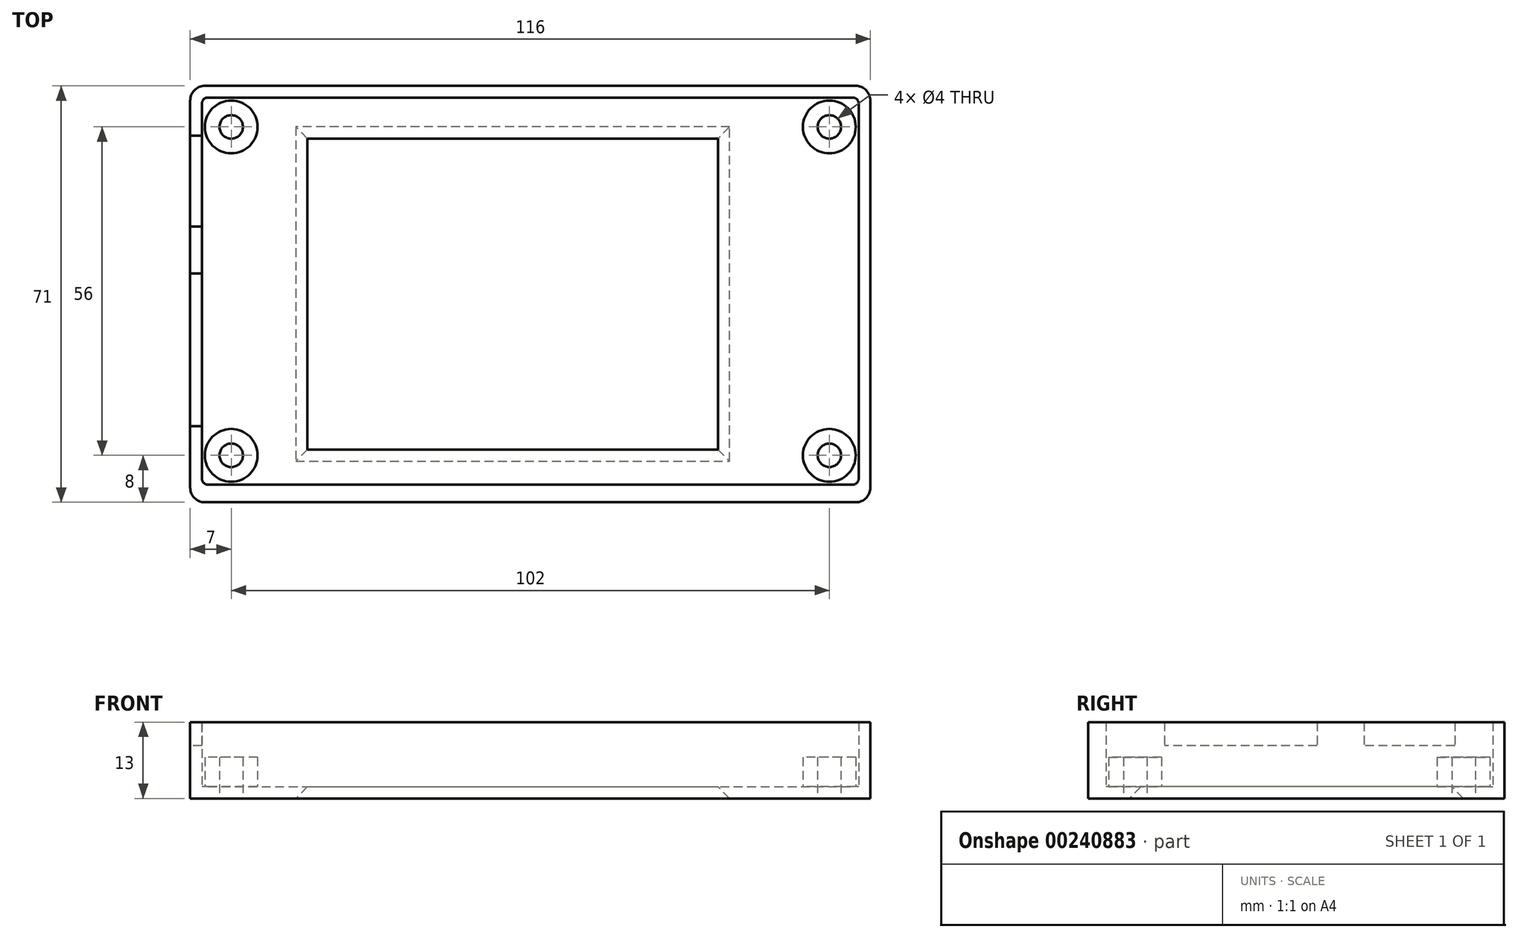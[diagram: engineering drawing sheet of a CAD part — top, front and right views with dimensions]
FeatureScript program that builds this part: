
annotation { "Feature Type Name" : "Feature", "Feature Type Description" : "" }
export const myFeature = defineFeature(function(context is Context, id is Id, definition is map)
    precondition{}
    {
        {
            var Q0;
            Q0=qCreatedBy(makeId("Top.planeOp"),FACE);
            var sketch = newSketch(context, id + "F0", { "sketchPlane" : qUnion([Q0])});
            skLineSegment(sketch, "E0.bottom", {"start": v(0, 71) * mm, "end": v(116, 71) * mm});
            skLineSegment(sketch, "E0.top", {"start": v(0, 0) * mm, "end": v(116, 0) * mm});
            skLineSegment(sketch, "E0.left", {"start": v(0, 71) * mm, "end": v(0, 0) * mm});
            skLineSegment(sketch, "E0.right", {"start": v(116, 71) * mm, "end": v(116, 0) * mm});
            skLineSegment(sketch, "E1.bottom", {"start": v(20, 9) * mm, "end": v(90, 9) * mm});
            skLineSegment(sketch, "E1.top", {"start": v(20, 62) * mm, "end": v(90, 62) * mm});
            skLineSegment(sketch, "E1.left", {"start": v(20, 62) * mm, "end": v(20, 9) * mm});
            skLineSegment(sketch, "E1.right", {"start": v(90, 62) * mm, "end": v(90, 9) * mm});
            skSolve(sketch);
        }
        {
            var Q0;
            Q0=makeQuery(id+"F0.imprint","IMPRINT",FACE,{"disambiguationData":[TD([[makeQuery(id+"F0.imprint","IMPRINT",EDGE,{"derivedFrom":sQuery(id+"F0.wireOp",EDGE,"E0.bottom")}),-1.0]])]});
            extrude(context, id + "F1", {"entities" : qUnion([Q0]), "depth" : 2 * mm});
        }
        {
            var Q0;
            Q0=makeQuery(id+"F1.opExtrude","CAP_FACE",FACE,{"disambiguationData":[OSD([sQuery(id+"F0.wireOp",EDGE,"E0.bottom"),sQuery(id+"F0.wireOp",EDGE,"E0.top"),sQuery(id+"F0.wireOp",EDGE,"E0.left"),sQuery(id+"F0.wireOp",EDGE,"E0.right"),sQuery(id+"F0.wireOp",EDGE,"E1.bottom"),sQuery(id+"F0.wireOp",EDGE,"E1.top"),sQuery(id+"F0.wireOp",EDGE,"E1.left"),sQuery(id+"F0.wireOp",EDGE,"E1.right")])],"isStart":false});
            var sketch = newSketch(context, id + "F2", { "sketchPlane" : qUnion([Q0])});
            skLineSegment(sketch, "E2.bottom", {"start": v(0, 71) * mm, "end": v(116, 71) * mm});
            skLineSegment(sketch, "E2.top", {"start": v(0, 0) * mm, "end": v(116, 0) * mm});
            skLineSegment(sketch, "E2.left", {"start": v(0, 71) * mm, "end": v(0, 0) * mm});
            skLineSegment(sketch, "E2.right", {"start": v(116, 71) * mm, "end": v(116, 0) * mm});
            skLineSegment(sketch, "E3.bottom", {"start": v(2, 69) * mm, "end": v(114, 69) * mm});
            skLineSegment(sketch, "E3.top", {"start": v(2, 3) * mm, "end": v(114, 3) * mm});
            skLineSegment(sketch, "E3.left", {"start": v(2, 69) * mm, "end": v(2, 3) * mm});
            skLineSegment(sketch, "E3.right", {"start": v(114, 69) * mm, "end": v(114, 3) * mm});
            skSolve(sketch);
        }
        {
            var Q0;
            Q0 = qSketchRegion(id + "F2", true);
            extrude(context, id + "F3", {"entities" : qUnion([Q0]), "operationType" : NewBodyOperationType.ADD, "depth" : 11 * mm});
        }
        {
            var Q0;
            Q0=makeQuery(id+"F3.boolean.opBoolean","MERGE",EDGE,{"derivedFrom":[makeQuery(id+"F1.opExtrude","SWEPT_EDGE",EDGE,{"disambiguationData":[OSD([sQuery(id+"F0.wireOp",EDGE,"E0.top"),sQuery(id+"F0.wireOp",EDGE,"E0.left")])]}),makeQuery(id+"F3.opExtrude","SWEPT_EDGE",EDGE,{"disambiguationData":[OSD([sQuery(id+"F2.wireOp",EDGE,"E2.top"),sQuery(id+"F2.wireOp",EDGE,"E2.left")])]})]});
            var Q1;
            Q1=makeQuery(id+"F3.boolean.opBoolean","MERGE",EDGE,{"derivedFrom":[makeQuery(id+"F1.opExtrude","SWEPT_EDGE",EDGE,{"disambiguationData":[OSD([sQuery(id+"F0.wireOp",EDGE,"E0.top"),sQuery(id+"F0.wireOp",EDGE,"E0.right")])]}),makeQuery(id+"F3.opExtrude","SWEPT_EDGE",EDGE,{"disambiguationData":[OSD([sQuery(id+"F2.wireOp",EDGE,"E2.top"),sQuery(id+"F2.wireOp",EDGE,"E2.right")])]})]});
            var Q2;
            Q2=makeQuery(id+"F3.boolean.opBoolean","MERGE",EDGE,{"derivedFrom":[makeQuery(id+"F1.opExtrude","SWEPT_EDGE",EDGE,{"disambiguationData":[OSD([sQuery(id+"F0.wireOp",EDGE,"E0.bottom"),sQuery(id+"F0.wireOp",EDGE,"E0.left")])]}),makeQuery(id+"F3.opExtrude","SWEPT_EDGE",EDGE,{"disambiguationData":[OSD([sQuery(id+"F2.wireOp",EDGE,"E2.bottom"),sQuery(id+"F2.wireOp",EDGE,"E2.left")])]})]});
            var Q3;
            Q3=makeQuery(id+"F3.boolean.opBoolean","MERGE",EDGE,{"derivedFrom":[makeQuery(id+"F1.opExtrude","SWEPT_EDGE",EDGE,{"disambiguationData":[OSD([sQuery(id+"F0.wireOp",EDGE,"E0.bottom"),sQuery(id+"F0.wireOp",EDGE,"E0.right")])]}),makeQuery(id+"F3.opExtrude","SWEPT_EDGE",EDGE,{"disambiguationData":[OSD([sQuery(id+"F2.wireOp",EDGE,"E2.bottom"),sQuery(id+"F2.wireOp",EDGE,"E2.right")])]})]});
            fillet(context, id + "F4", {"entities" : qUnion([Q0, Q1, Q2, Q3]), "radius" : 2.5 * mm, "tangentPropagation" : true, "allowEdgeOverflow" : false});
        }
        {
            var Q0;
            Q0=makeQuery(id+"F3.opExtrude","SWEPT_EDGE",EDGE,{"disambiguationData":[OSD([sQuery(id+"F2.wireOp",EDGE,"E3.top"),sQuery(id+"F2.wireOp",EDGE,"E3.right")])]});
            var Q1;
            Q1=makeQuery(id+"F3.opExtrude","SWEPT_EDGE",EDGE,{"disambiguationData":[OSD([sQuery(id+"F2.wireOp",EDGE,"E3.top"),sQuery(id+"F2.wireOp",EDGE,"E3.left")])]});
            var Q2;
            Q2=makeQuery(id+"F3.opExtrude","SWEPT_EDGE",EDGE,{"disambiguationData":[OSD([sQuery(id+"F2.wireOp",EDGE,"E3.bottom"),sQuery(id+"F2.wireOp",EDGE,"E3.left")])]});
            var Q3;
            Q3=makeQuery(id+"F3.opExtrude","SWEPT_EDGE",EDGE,{"disambiguationData":[OSD([sQuery(id+"F2.wireOp",EDGE,"E3.bottom"),sQuery(id+"F2.wireOp",EDGE,"E3.right")])]});
            fillet(context, id + "F5", {"entities" : qUnion([Q0, Q1, Q2, Q3]), "radius" : 1 * mm, "tangentPropagation" : true, "allowEdgeOverflow" : false});
        }
        {
            var Q0;
            Q0=makeQuery(id+"F2.imprint","IMPRINT",FACE,{"disambiguationData":[TD([[makeQuery(id+"F2.imprint","IMPRINT",EDGE,{"derivedFrom":sQuery(id+"F2.wireOp",EDGE,"E3.bottom")}),-1.0]])]});
            var sketch = newSketch(context, id + "F6", { "sketchPlane" : qUnion([Q0])});
            skCircle(sketch, "E4", {"center": v(7, 64) * mm, "radius": 4.5 * mm});
            skCircle(sketch, "E5", {"center": v(7, 8) * mm, "radius": 4.5 * mm});
            skCircle(sketch, "E6", {"center": v(109, 8) * mm, "radius": 4.5 * mm});
            skCircle(sketch, "E7", {"center": v(109, 64) * mm, "radius": 4.5 * mm});
            skCircle(sketch, "E8", {"center": v(7, 64) * mm, "radius": 2 * mm});
            skCircle(sketch, "E9", {"center": v(7, 8) * mm, "radius": 2 * mm});
            skCircle(sketch, "E10", {"center": v(109, 64) * mm, "radius": 2 * mm});
            skCircle(sketch, "E11", {"center": v(109, 8) * mm, "radius": 2 * mm});
            skSolve(sketch);
        }
        {
            var Q0;
            Q0 = qSketchRegion(id + "F6", true);
            extrude(context, id + "F7", {"entities" : qUnion([Q0]), "operationType" : NewBodyOperationType.ADD, "depth" : 5 * mm});
        }
        {
            var Q0;
            Q0=makeQuery(id+"F1.opExtrude","CAP_EDGE",EDGE,{"disambiguationData":[OSD([sQuery(id+"F0.wireOp",EDGE,"E1.right")])],"isStart":true});
            var Q1;
            Q1=makeQuery(id+"F1.opExtrude","CAP_EDGE",EDGE,{"disambiguationData":[OSD([sQuery(id+"F0.wireOp",EDGE,"E1.bottom")])],"isStart":true});
            var Q2;
            Q2=makeQuery(id+"F1.opExtrude","CAP_EDGE",EDGE,{"disambiguationData":[OSD([sQuery(id+"F0.wireOp",EDGE,"E1.left")])],"isStart":true});
            var Q3;
            Q3=makeQuery(id+"F1.opExtrude","CAP_EDGE",EDGE,{"disambiguationData":[OSD([sQuery(id+"F0.wireOp",EDGE,"E1.top")])],"isStart":true});
            chamfer(context, id + "F8", {"entities" : qUnion([Q0, Q1, Q2, Q3]), "width" : 2 * mm, "tangentPropagation" : true});
        }
        {
            var Q0;
            Q0=makeQuery(id+"F3.boolean.opBoolean","MERGE",FACE,{"derivedFrom":[makeQuery(id+"F1.opExtrude","SWEPT_FACE",FACE,{"disambiguationData":[OSD([sQuery(id+"F0.wireOp",EDGE,"E0.left")])]}),makeQuery(id+"F3.opExtrude","SWEPT_FACE",FACE,{"disambiguationData":[OSD([sQuery(id+"F2.wireOp",EDGE,"E2.left")])]})]});
            var sketch = newSketch(context, id + "F9", { "sketchPlane" : qUnion([Q0])});
            skLineSegment(sketch, "E12.bottom", {"start": v(-62.5, 16.5) * mm, "end": v(-47, 16.5) * mm});
            skLineSegment(sketch, "E12.top", {"start": v(-62.5, 9) * mm, "end": v(-47, 9) * mm});
            skLineSegment(sketch, "E12.left", {"start": v(-62.5, 16.5) * mm, "end": v(-62.5, 9) * mm});
            skLineSegment(sketch, "E12.right", {"start": v(-47, 16.5) * mm, "end": v(-47, 9) * mm});
            skLineSegment(sketch, "E13.bottom", {"start": v(-39, 13) * mm, "end": v(-13, 13) * mm});
            skLineSegment(sketch, "E13.top", {"start": v(-39, 9) * mm, "end": v(-13, 9) * mm});
            skLineSegment(sketch, "E13.left", {"start": v(-39, 13) * mm, "end": v(-39, 9) * mm});
            skLineSegment(sketch, "E13.right", {"start": v(-13, 13) * mm, "end": v(-13, 9) * mm});
            skSolve(sketch);
        }
        {
            var Q0;
            Q0 = qSketchRegion(id + "F9", true);
            extrude(context, id + "F10", {"entities" : qUnion([Q0]), "operationType" : NewBodyOperationType.REMOVE, "oppositeDirection" : true, "depth" : 25 * mm});
        }
        {
            var Q0;
            Q0=makeQuery(id+"F7.boolean.opBoolean","SPLIT",FACE,{"disambiguationData":[TD([makeQuery(id+"F7.opExtrude","SWEPT_FACE",FACE,{"disambiguationData":[OSD([sQuery(id+"F6.wireOp",EDGE,"E9")])]})])],"derivedFrom":makeQuery(id+"F1.opExtrude","CAP_FACE",FACE,{"disambiguationData":[OSD([sQuery(id+"F0.wireOp",EDGE,"E0.bottom"),sQuery(id+"F0.wireOp",EDGE,"E0.top"),sQuery(id+"F0.wireOp",EDGE,"E0.left"),sQuery(id+"F0.wireOp",EDGE,"E0.right"),sQuery(id+"F0.wireOp",EDGE,"E1.bottom"),sQuery(id+"F0.wireOp",EDGE,"E1.top"),sQuery(id+"F0.wireOp",EDGE,"E1.left"),sQuery(id+"F0.wireOp",EDGE,"E1.right")])],"isStart":false})});
            var Q1;
            Q1=makeQuery(id+"F7.boolean.opBoolean","SPLIT",FACE,{"disambiguationData":[TD([makeQuery(id+"F7.opExtrude","SWEPT_FACE",FACE,{"disambiguationData":[OSD([sQuery(id+"F6.wireOp",EDGE,"E8")])]})])],"derivedFrom":makeQuery(id+"F1.opExtrude","CAP_FACE",FACE,{"disambiguationData":[OSD([sQuery(id+"F0.wireOp",EDGE,"E0.bottom"),sQuery(id+"F0.wireOp",EDGE,"E0.top"),sQuery(id+"F0.wireOp",EDGE,"E0.left"),sQuery(id+"F0.wireOp",EDGE,"E0.right"),sQuery(id+"F0.wireOp",EDGE,"E1.bottom"),sQuery(id+"F0.wireOp",EDGE,"E1.top"),sQuery(id+"F0.wireOp",EDGE,"E1.left"),sQuery(id+"F0.wireOp",EDGE,"E1.right")])],"isStart":false})});
            var Q2;
            Q2=makeQuery(id+"F7.boolean.opBoolean","SPLIT",FACE,{"disambiguationData":[TD([makeQuery(id+"F7.opExtrude","SWEPT_FACE",FACE,{"disambiguationData":[OSD([sQuery(id+"F6.wireOp",EDGE,"E11")])]})])],"derivedFrom":makeQuery(id+"F1.opExtrude","CAP_FACE",FACE,{"disambiguationData":[OSD([sQuery(id+"F0.wireOp",EDGE,"E0.bottom"),sQuery(id+"F0.wireOp",EDGE,"E0.top"),sQuery(id+"F0.wireOp",EDGE,"E0.left"),sQuery(id+"F0.wireOp",EDGE,"E0.right"),sQuery(id+"F0.wireOp",EDGE,"E1.bottom"),sQuery(id+"F0.wireOp",EDGE,"E1.top"),sQuery(id+"F0.wireOp",EDGE,"E1.left"),sQuery(id+"F0.wireOp",EDGE,"E1.right")])],"isStart":false})});
            var Q3;
            Q3=makeQuery(id+"F7.boolean.opBoolean","SPLIT",FACE,{"disambiguationData":[TD([makeQuery(id+"F7.opExtrude","SWEPT_FACE",FACE,{"disambiguationData":[OSD([sQuery(id+"F6.wireOp",EDGE,"E10")])]})])],"derivedFrom":makeQuery(id+"F1.opExtrude","CAP_FACE",FACE,{"disambiguationData":[OSD([sQuery(id+"F0.wireOp",EDGE,"E0.bottom"),sQuery(id+"F0.wireOp",EDGE,"E0.top"),sQuery(id+"F0.wireOp",EDGE,"E0.left"),sQuery(id+"F0.wireOp",EDGE,"E0.right"),sQuery(id+"F0.wireOp",EDGE,"E1.bottom"),sQuery(id+"F0.wireOp",EDGE,"E1.top"),sQuery(id+"F0.wireOp",EDGE,"E1.left"),sQuery(id+"F0.wireOp",EDGE,"E1.right")])],"isStart":false})});
            var Q4;
            Q4=sQuery(id+"F6.wireOp",EDGE,"E8");
            var Q5;
            Q5=sQuery(id+"F6.wireOp",EDGE,"E9");
            var Q6;
            Q6=sQuery(id+"F6.wireOp",EDGE,"E11");
            var Q7;
            Q7=sQuery(id+"F6.wireOp",EDGE,"E10");
            extrude(context, id + "F11", {"entities" : qUnion([Q0, Q1, Q2, Q3]), "operationType" : NewBodyOperationType.REMOVE, "surfaceEntities" : qUnion([Q4, Q5, Q6, Q7]), "oppositeDirection" : true, "depth" : 25 * mm});
        }
    });
